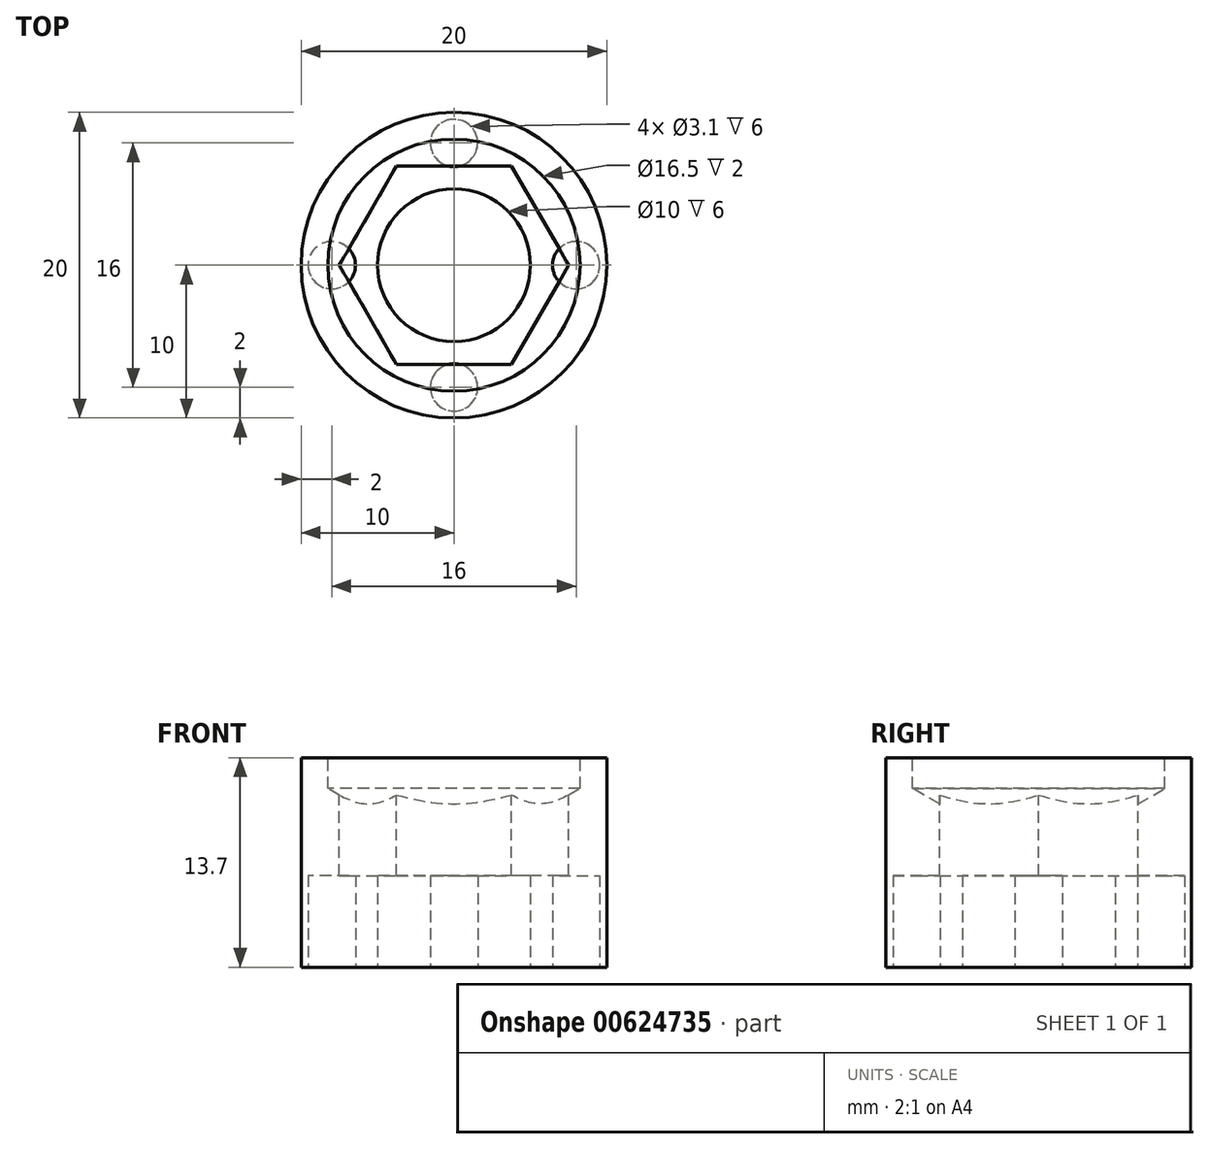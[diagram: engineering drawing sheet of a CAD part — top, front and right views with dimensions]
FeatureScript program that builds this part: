
annotation { "Feature Type Name" : "Feature", "Feature Type Description" : "" }
export const myFeature = defineFeature(function(context is Context, id is Id, definition is map)
    precondition{}
    {
        {
            var Q0;
            Q0=qCreatedBy(makeId("Top.planeOp"),FACE);
            var sketch = newSketch(context, id + "F0", { "sketchPlane" : qUnion([Q0])});
            skCircle(sketch, "E0", {"center": v(0, 0) * mm, "radius": 10 * mm});
            skSolve(sketch);
        }
        {
            var Q0;
            Q0=qSketchRegion(id+"F0",true);
            extrude(context, id + "F1", {"entities" : qUnion([Q0]), "depth" : 13.7 * mm});
        }
        {
            var Q0;
            Q0=makeQuery(id+"F1.opExtrude","CAP_FACE",FACE,{"disambiguationData":[OSD([sQuery(id+"F0.wireOp",EDGE,"E0"),sQuery(id+"F0.wireOp",EDGE,"fjR7CbzK-vdTR-2RCl-wO5z-ya975b1oAJkp"),sQuery(id+"F0.wireOp",EDGE,"bd624da8-9536-46e7-ae97-a14b9787860a0.MirrorC"),sQuery(id+"F0.wireOp",EDGE,"fXrsHEft-Bsd9-onXM-nepM-QBil7Rs2XQ31"),sQuery(id+"F0.wireOp",EDGE,"53074977-7981-4dbe-9476-5fdd181049810.MirrorC")])],"isStart":false});
            var sketch = newSketch(context, id + "F2", { "sketchPlane" : qUnion([Q0])});
            skCircle(sketch, "E1.cCircle", {"center": v(0, 0) * mm, "radius": 6.5 * mm, "construction": true});
            skLineSegment(sketch, "E1.0", {"start": v(-3.75, 6.5) * mm, "end": v(3.75, 6.5) * mm});
            skLineSegment(sketch, "E1.1", {"start": v(3.75, 6.5) * mm, "end": v(7.5, 0) * mm});
            skLineSegment(sketch, "E1.2", {"start": v(7.5, 0) * mm, "end": v(3.75, -6.5) * mm});
            skLineSegment(sketch, "E1.3", {"start": v(3.75, -6.5) * mm, "end": v(-3.75, -6.5) * mm});
            skLineSegment(sketch, "E1.4", {"start": v(-3.75, -6.5) * mm, "end": v(-7.5, 0) * mm});
            skLineSegment(sketch, "E1.5", {"start": v(-7.5, 0) * mm, "end": v(-3.75, 6.5) * mm});
            skPoint(sketch, "E1.0.midPoint", {"position": v(0, 6.5) * mm});
            skSolve(sketch);
        }
        {
            var Q0;
            Q0=qSketchRegion(id+"F2",true);
            extrude(context, id + "F3", {"entities" : qUnion([Q0]), "operationType" : NewBodyOperationType.REMOVE, "oppositeDirection" : true, "depth" : 7.7 * mm});
        }
        {
            var Q0;
            Q0=qCreatedBy(makeId("Right.planeOp"),FACE);
            var sketch = newSketch(context, id + "F4", { "sketchPlane" : qUnion([Q0])});
            skLineSegment(sketch, "E2", {"start": v(0, 13.7) * mm, "end": v(8.25, 13.7) * mm});
            skLineSegment(sketch, "E3", {"start": v(8.25, 13.7) * mm, "end": v(8.25, 11.7) * mm});
            skLineSegment(sketch, "E4", {"start": v(8.25, 11.7) * mm, "end": v(6.5, 10.7) * mm});
            skLineSegment(sketch, "E5", {"start": v(6.5, 10.7) * mm, "end": v(0, 10.7) * mm});
            skLineSegment(sketch, "E6", {"start": v(0, 10.7) * mm, "end": v(0, 13.7) * mm});
            skSolve(sketch);
        }
        {
            var Q0;
            Q0=makeQuery(id+"F1.opExtrude","CAP_FACE",FACE,{"disambiguationData":[OSD([sQuery(id+"F0.wireOp",EDGE,"E0")])],"isStart":true});
            var sketch = newSketch(context, id + "F5", { "sketchPlane" : qUnion([Q0])});
            skCircle(sketch, "E7", {"center": v(0, 8) * mm, "radius": 1.55 * mm});
            skCircle(sketch, "E8.MirrorC", {"center": v(0, -8) * mm, "radius": 1.55 * mm});
            skCircle(sketch, "E9", {"center": v(8, 0) * mm, "radius": 1.55 * mm});
            skCircle(sketch, "E10.MirrorC", {"center": v(-8, 0) * mm, "radius": 1.55 * mm});
            skSolve(sketch);
        }
        {
            var Q0;
            Q0=qSketchRegion(id+"F5",true);
            extrude(context, id + "F6", {"entities" : qUnion([Q0]), "operationType" : NewBodyOperationType.REMOVE, "oppositeDirection" : true, "depth" : 6 * mm});
        }
        {
            var Q0;
            Q0=qSketchRegion(id+"F4",true);
            var Q1;
            Q1=sQuery(id+"F4.wireOp",EDGE,"E6");
            revolve(context, id + "F7", {"operationType" : NewBodyOperationType.REMOVE, "entities" : qUnion([Q0]), "axis" : qUnion([Q1]), "revolveType" : RevolveType.FULL, "oppositeDirection" : true});
        }
        {
            var Q0;
            Q0=makeQuery(id+"F1.opExtrude","CAP_FACE",FACE,{"disambiguationData":[OSD([sQuery(id+"F0.wireOp",EDGE,"E0")])],"isStart":true});
            var sketch = newSketch(context, id + "F8", { "sketchPlane" : qUnion([Q0])});
            skCircle(sketch, "E11", {"center": v(0, 0) * mm, "radius": 5 * mm});
            skSolve(sketch);
        }
        {
            var Q0;
            Q0=qSketchRegion(id+"F8",true);
            extrude(context, id + "F9", {"entities" : qUnion([Q0]), "operationType" : NewBodyOperationType.REMOVE, "oppositeDirection" : true, "depth" : 25 * mm});
        }
    });
